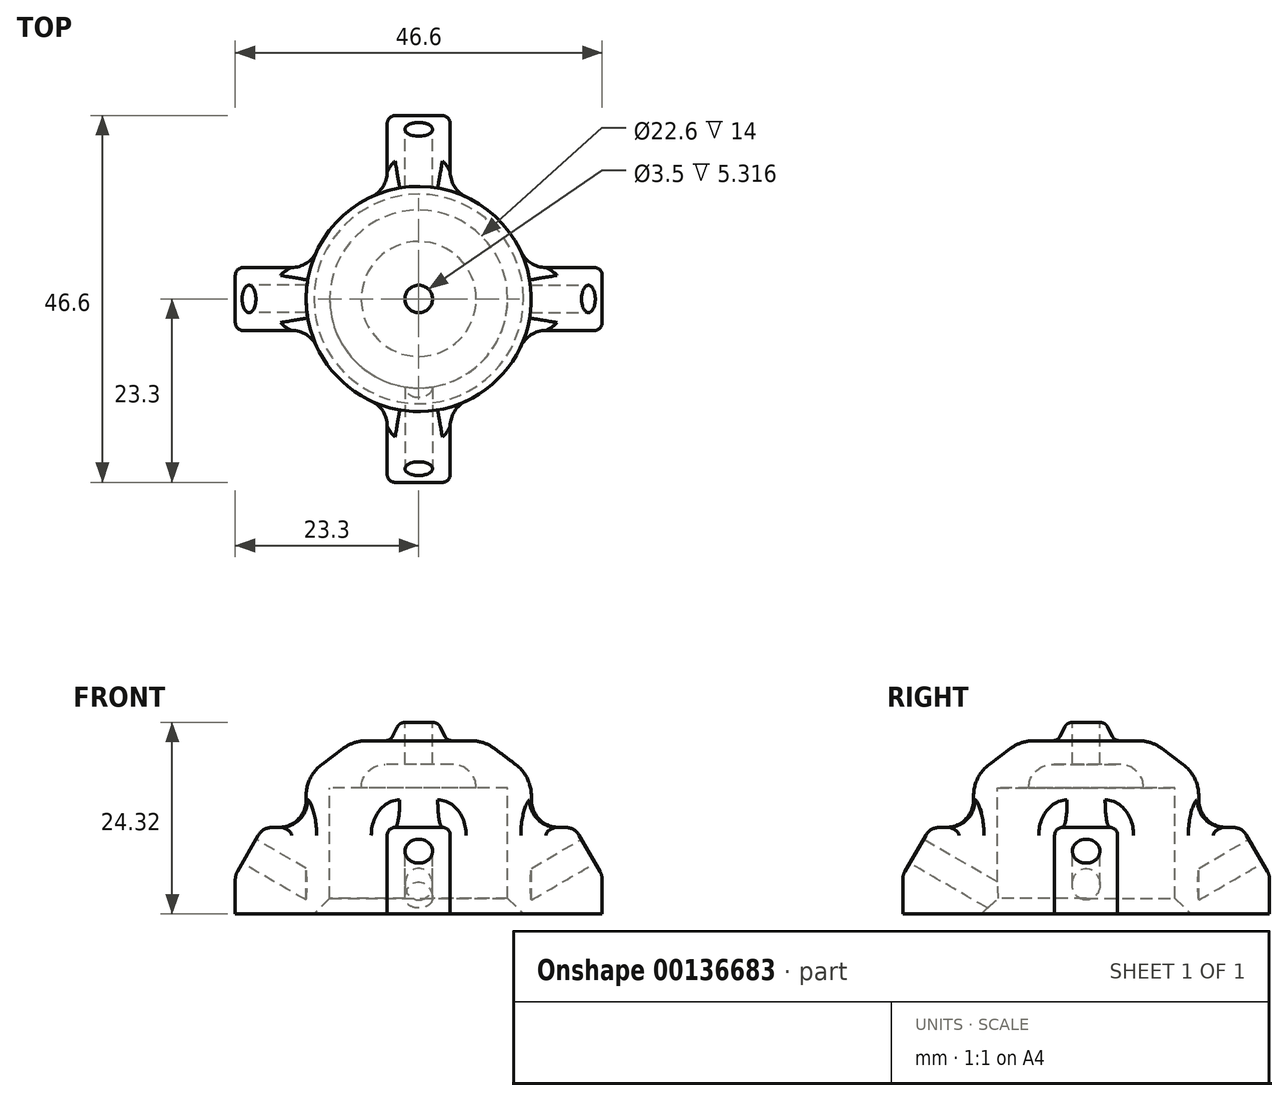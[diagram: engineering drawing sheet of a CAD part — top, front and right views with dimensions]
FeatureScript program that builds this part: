
annotation { "Feature Type Name" : "Feature", "Feature Type Description" : "" }
export const myFeature = defineFeature(function(context is Context, id is Id, definition is map)
    precondition{}
    {
        {
            var Q0;
            Q0=qCreatedBy(makeId("Right.planeOp"),FACE);
            var sketch = newSketch(context, id + "F0", { "sketchPlane" : qUnion([Q0])});
            skLineSegment(sketch, "E0", {"start": v(-11.3, 0) * mm, "end": v(-11.3, 16) * mm});
            skLineSegment(sketch, "E1", {"start": v(-11.3, 16) * mm, "end": v(-7.3, 16) * mm});
            skLineSegment(sketch, "E2", {"start": v(-7.3, 16) * mm, "end": v(-7.3, 19) * mm});
            skLineSegment(sketch, "E3", {"start": v(-14.3, 0) * mm, "end": v(-11.3, 0) * mm});
            skLineSegment(sketch, "E4", {"start": v(-14.3, 0) * mm, "end": v(-14.3, 17.5) * mm});
            skLineSegment(sketch, "E5", {"start": v(-14.3, 17.5) * mm, "end": v(-8.3, 22) * mm});
            skLineSegment(sketch, "E6", {"start": v(-8.3, 22) * mm, "end": v(0, 22) * mm});
            skLineSegment(sketch, "E7", {"start": v(0, 22) * mm, "end": v(0, 19) * mm});
            skLineSegment(sketch, "E8", {"start": v(0, 19) * mm, "end": v(-7.3, 19) * mm});
            skLineSegment(sketch, "E9", {"start": v(-7.3, 19) * mm, "end": v(-11.3, 16) * mm, "construction": true});
            skLineSegment(sketch, "E10", {"start": v(-3.6, 22) * mm, "end": v(-2.45, 24.32) * mm});
            skLineSegment(sketch, "E11", {"start": v(-2.45, 24.32) * mm, "end": v(0, 24.32) * mm});
            skLineSegment(sketch, "E12", {"start": v(0, 24.32) * mm, "end": v(0, 22) * mm});
            skSolve(sketch);
        }
        {
            var Q0;
            Q0 = qSketchRegion(id + "F0", true);
            var Q1;
            Q1=sQuery(id+"F0.wireOp",EDGE,"E7");
            revolve(context, id + "F1", {"entities" : qUnion([Q0]), "axis" : qUnion([Q1]), "revolveType" : RevolveType.FULL});
        }
        {
            var Q0;
            Q0=makeQuery(id+"F1.opRevolve","SWEPT_FACE",FACE,{"disambiguationData":[OSD([sQuery(id+"F0.wireOp",EDGE,"E6")])]});
            var sketch = newSketch(context, id + "F2", { "sketchPlane" : qUnion([Q0])});
            skCircle(sketch, "E13", {"center": v(0, 0) * mm, "radius": 1.75 * mm});
            skSolve(sketch);
        }
        {
            var Q0;
            Q0 = qSketchRegion(id + "F2", true);
            var Q1;
            Q1=makeQuery(id+"F1.opRevolve","SWEPT_FACE",FACE,{"disambiguationData":[OSD([sQuery(id+"F0.wireOp",EDGE,"E8")])]});
            extrude(context, id + "F3", {"entities" : qUnion([Q0]), "operationType" : NewBodyOperationType.REMOVE, "endBound" : BoundingType.SYMMETRIC, "oppositeDirection" : true, "endBoundEntityFace" : qUnion([Q1]), "depth" : 25 * mm});
        }
        {
            var Q0;
            Q0=qCreatedBy(makeId("Right.planeOp"),FACE);
            var sketch = newSketch(context, id + "F4", { "sketchPlane" : qUnion([Q0])});
            skLineSegment(sketch, "E14", {"start": v(-11.3, 0) * mm, "end": v(-11.3, 11) * mm});
            skLineSegment(sketch, "E15", {"start": v(-11.3, 11) * mm, "end": v(-19.8, 11) * mm});
            skLineSegment(sketch, "E16", {"start": v(-19.8, 11) * mm, "end": v(-23.3, 4.94) * mm});
            skLineSegment(sketch, "E17", {"start": v(-23.3, 4.94) * mm, "end": v(-23.3, 0) * mm});
            skLineSegment(sketch, "E18", {"start": v(-23.3, 0) * mm, "end": v(-11.3, 0) * mm});
            skLineSegment(sketch, "E19.0", {"start": v(-11.3, 0) * mm, "end": v(11.3, 0) * mm, "construction": true});
            skSolve(sketch);
        }
        {
            var Q0;
            Q0 = qSketchRegion(id + "F4", true);
            extrude(context, id + "F5", {"entities" : qUnion([Q0]), "endBound" : BoundingType.SYMMETRIC, "depth" : 8 * mm});
        }
        {
            var Q0;
            Q0=makeQuery(id+"F5.opExtrude","SWEPT_FACE",FACE,{"disambiguationData":[OSD([sQuery(id+"F4.wireOp",EDGE,"E16")])]});
            var sketch = newSketch(context, id + "F6", { "sketchPlane" : qUnion([Q0])});
            skCircle(sketch, "E20", {"center": v(0, -3.87) * mm, "radius": 1.75 * mm});
            skPoint(sketch, "E20.centerSnap0", {"position": v(4, -3.87) * mm});
            skSolve(sketch);
        }
        {
            var Q0;
            Q0 = qSketchRegion(id + "F6", true);
            extrude(context, id + "F7", {"entities" : qUnion([Q0]), "operationType" : NewBodyOperationType.REMOVE, "endBound" : BoundingType.THROUGH_ALL, "oppositeDirection" : true, "depth" : 25 * mm});
        }
        {
            var Q0;
            Q0=makeQuery(id+"F5.opExtrude","SWEPT_EDGE",EDGE,{"disambiguationData":[OSD([sQuery(id+"F4.wireOp",EDGE,"E16"),sQuery(id+"F4.wireOp",EDGE,"E17")])]});
            var Q1;
            Q1=makeQuery(id+"F5.opExtrude","SWEPT_EDGE",EDGE,{"disambiguationData":[OSD([sQuery(id+"F4.wireOp",EDGE,"E15"),sQuery(id+"F4.wireOp",EDGE,"E16")])]});
            fillet(context, id + "F8", {"entities" : qUnion([Q0, Q1]), "radius" : 2 * mm, "tangentPropagation" : true, "allowEdgeOverflow" : false});
        }
        {
            var Q0;
            Q0=makeQuery(id+"F5.opExtrude","CAP_EDGE",EDGE,{"disambiguationData":[OSD([sQuery(id+"F4.wireOp",EDGE,"E17")])],"isStart":false});
            var Q1;
            Q1=makeQuery(id+"F5.opExtrude","CAP_EDGE",EDGE,{"disambiguationData":[OSD([sQuery(id+"F4.wireOp",EDGE,"E17")])],"isStart":true});
            fillet(context, id + "F9", {"entities" : qUnion([Q0, Q1]), "radius" : 1 * mm, "tangentPropagation" : true, "allowEdgeOverflow" : false});
        }
        {
            var Q0;
            Q0=makeQuery(id+"F5.opExtrude","SWEPT_BODY",BODY,{"disambiguationData":[OSD([sQuery(id+"F4.wireOp",EDGE,"E14"),sQuery(id+"F4.wireOp",EDGE,"E15"),sQuery(id+"F4.wireOp",EDGE,"E16"),sQuery(id+"F4.wireOp",EDGE,"E17"),sQuery(id+"F4.wireOp",EDGE,"E18")])]});
            var Q1;
            Q1=makeQuery(id+"F1.opRevolve","SWEPT_EDGE",EDGE,{"disambiguationData":[OSD([sQuery(id+"F0.wireOp",EDGE,"E0"),sQuery(id+"F0.wireOp",EDGE,"E3")])]});
            circularPattern(context, id + "F10", {"entities" : qUnion([Q0]), "axis" : qUnion([Q1]), "angle" : 360 * degree, "instanceCount" : 4, "equalSpace" : true});
        }
        {
            var Q0;
            Q0=makeQuery(id+"F1.opRevolve","SWEPT_BODY",BODY,{"disambiguationData":[OSD([sQuery(id+"F0.wireOp",EDGE,"E0"),sQuery(id+"F0.wireOp",EDGE,"E1"),sQuery(id+"F0.wireOp",EDGE,"E2"),sQuery(id+"F0.wireOp",EDGE,"E3"),sQuery(id+"F0.wireOp",EDGE,"E4"),sQuery(id+"F0.wireOp",EDGE,"E5"),sQuery(id+"F0.wireOp",EDGE,"E6"),sQuery(id+"F0.wireOp",EDGE,"E7"),sQuery(id+"F0.wireOp",EDGE,"E8")])]});
            var Q1;
            Q1=makeQuery(id+"F5.opExtrude","SWEPT_BODY",BODY,{"disambiguationData":[OSD([sQuery(id+"F4.wireOp",EDGE,"E14"),sQuery(id+"F4.wireOp",EDGE,"E15"),sQuery(id+"F4.wireOp",EDGE,"E16"),sQuery(id+"F4.wireOp",EDGE,"E17"),sQuery(id+"F4.wireOp",EDGE,"E18")])]});
            var Q2;
            Q2=makeQuery(id+"F10.opPattern","COPY",BODY,{"derivedFrom":makeQuery(id+"F5.opExtrude","SWEPT_BODY",BODY,{"disambiguationData":[OSD([sQuery(id+"F4.wireOp",EDGE,"E14"),sQuery(id+"F4.wireOp",EDGE,"E15"),sQuery(id+"F4.wireOp",EDGE,"E16"),sQuery(id+"F4.wireOp",EDGE,"E17"),sQuery(id+"F4.wireOp",EDGE,"E18")])]}),"instanceName":"1"});
            var Q3;
            Q3=makeQuery(id+"F10.opPattern","COPY",BODY,{"derivedFrom":makeQuery(id+"F5.opExtrude","SWEPT_BODY",BODY,{"disambiguationData":[OSD([sQuery(id+"F4.wireOp",EDGE,"E14"),sQuery(id+"F4.wireOp",EDGE,"E15"),sQuery(id+"F4.wireOp",EDGE,"E16"),sQuery(id+"F4.wireOp",EDGE,"E17"),sQuery(id+"F4.wireOp",EDGE,"E18")])]}),"instanceName":"2"});
            var Q4;
            Q4=makeQuery(id+"F10.opPattern","COPY",BODY,{"derivedFrom":makeQuery(id+"F5.opExtrude","SWEPT_BODY",BODY,{"disambiguationData":[OSD([sQuery(id+"F4.wireOp",EDGE,"E14"),sQuery(id+"F4.wireOp",EDGE,"E15"),sQuery(id+"F4.wireOp",EDGE,"E16"),sQuery(id+"F4.wireOp",EDGE,"E17"),sQuery(id+"F4.wireOp",EDGE,"E18")])]}),"instanceName":"3"});
            booleanBodies(context, id + "F11", {"operationType" : BooleanOperationType.UNION, "tools" : qUnion([Q0, Q1, Q2, Q3, Q4])});
        }
        {
            var Q0;
            Q0=makeQuery(id+"F11.opBoolean","INTERSECT",EDGE,{"derivedFrom":[makeQuery(id+"F1.opRevolve","SWEPT_FACE",FACE,{"disambiguationData":[OSD([sQuery(id+"F0.wireOp",EDGE,"E4")])]}),makeQuery(id+"F5.opExtrude","CAP_FACE",FACE,{"disambiguationData":[OSD([sQuery(id+"F4.wireOp",EDGE,"E14"),sQuery(id+"F4.wireOp",EDGE,"E15"),sQuery(id+"F4.wireOp",EDGE,"E16"),sQuery(id+"F4.wireOp",EDGE,"E17"),sQuery(id+"F4.wireOp",EDGE,"E18")])],"isStart":false})]});
            var Q1;
            Q1=makeQuery(id+"F11.opBoolean","INTERSECT",EDGE,{"derivedFrom":[makeQuery(id+"F1.opRevolve","SWEPT_FACE",FACE,{"disambiguationData":[OSD([sQuery(id+"F0.wireOp",EDGE,"E4")])]}),makeQuery(id+"F10.opPattern","COPY",FACE,{"derivedFrom":makeQuery(id+"F5.opExtrude","CAP_FACE",FACE,{"disambiguationData":[OSD([sQuery(id+"F4.wireOp",EDGE,"E14"),sQuery(id+"F4.wireOp",EDGE,"E15"),sQuery(id+"F4.wireOp",EDGE,"E16"),sQuery(id+"F4.wireOp",EDGE,"E17"),sQuery(id+"F4.wireOp",EDGE,"E18")])],"isStart":false}),"instanceName":"1"})]});
            var Q2;
            Q2=makeQuery(id+"F11.opBoolean","INTERSECT",EDGE,{"derivedFrom":[makeQuery(id+"F1.opRevolve","SWEPT_FACE",FACE,{"disambiguationData":[OSD([sQuery(id+"F0.wireOp",EDGE,"E4")])]}),makeQuery(id+"F10.opPattern","COPY",FACE,{"derivedFrom":makeQuery(id+"F5.opExtrude","CAP_FACE",FACE,{"disambiguationData":[OSD([sQuery(id+"F4.wireOp",EDGE,"E14"),sQuery(id+"F4.wireOp",EDGE,"E15"),sQuery(id+"F4.wireOp",EDGE,"E16"),sQuery(id+"F4.wireOp",EDGE,"E17"),sQuery(id+"F4.wireOp",EDGE,"E18")])],"isStart":false}),"instanceName":"2"})]});
            var Q3;
            Q3=makeQuery(id+"F11.opBoolean","INTERSECT",EDGE,{"derivedFrom":[makeQuery(id+"F1.opRevolve","SWEPT_FACE",FACE,{"disambiguationData":[OSD([sQuery(id+"F0.wireOp",EDGE,"E4")])]}),makeQuery(id+"F10.opPattern","COPY",FACE,{"derivedFrom":makeQuery(id+"F5.opExtrude","CAP_FACE",FACE,{"disambiguationData":[OSD([sQuery(id+"F4.wireOp",EDGE,"E14"),sQuery(id+"F4.wireOp",EDGE,"E15"),sQuery(id+"F4.wireOp",EDGE,"E16"),sQuery(id+"F4.wireOp",EDGE,"E17"),sQuery(id+"F4.wireOp",EDGE,"E18")])],"isStart":false}),"instanceName":"3"})]});
            fillet(context, id + "F12", {"entities" : qUnion([Q0, Q1, Q2, Q3]), "radius" : 3.5 * mm, "tangentPropagation" : true, "allowEdgeOverflow" : false});
        }
        {
            var Q0;
            Q0=makeQuery(id+"F1.opRevolve","SWEPT_EDGE",EDGE,{"disambiguationData":[OSD([sQuery(id+"F0.wireOp",EDGE,"E5"),sQuery(id+"F0.wireOp",EDGE,"E6")])]});
            var Q1;
            Q1=makeQuery(id+"F1.opRevolve","SWEPT_EDGE",EDGE,{"disambiguationData":[OSD([sQuery(id+"F0.wireOp",EDGE,"E4"),sQuery(id+"F0.wireOp",EDGE,"E5")])]});
            fillet(context, id + "F13", {"entities" : qUnion([Q0, Q1]), "radius" : 5 * mm, "tangentPropagation" : true, "allowEdgeOverflow" : false});
        }
        {
            var Q0;
            Q0=makeQuery(id+"F1.opRevolve","SWEPT_EDGE",EDGE,{"disambiguationData":[OSD([sQuery(id+"F0.wireOp",EDGE,"E0"),sQuery(id+"F0.wireOp",EDGE,"E3")])]});
            chamfer(context, id + "F14", {"entities" : qUnion([Q0]), "width" : 2 * mm, "tangentPropagation" : true});
        }
        {
            var Q0;
            Q0=makeQuery(id+"F1.opRevolve","SWEPT_EDGE",EDGE,{"disambiguationData":[OSD([sQuery(id+"F0.wireOp",EDGE,"E6"),sQuery(id+"F0.wireOp",EDGE,"E10")])]});
            var Q1;
            Q1=makeQuery(id+"F1.opRevolve","SWEPT_EDGE",EDGE,{"disambiguationData":[OSD([sQuery(id+"F0.wireOp",EDGE,"E10"),sQuery(id+"F0.wireOp",EDGE,"E11")])]});
            fillet(context, id + "F15", {"entities" : qUnion([Q0, Q1]), "radius" : 1 * mm, "tangentPropagation" : true, "allowEdgeOverflow" : false});
        }
        {
            var Q0;
            Q0=makeQuery(id+"F1.opRevolve","SWEPT_EDGE",EDGE,{"disambiguationData":[OSD([sQuery(id+"F0.wireOp",EDGE,"E2"),sQuery(id+"F0.wireOp",EDGE,"E8")])]});
            fillet(context, id + "F16", {"entities" : qUnion([Q0]), "radius" : 3 * mm, "tangentPropagation" : true, "allowEdgeOverflow" : false});
        }
    });
